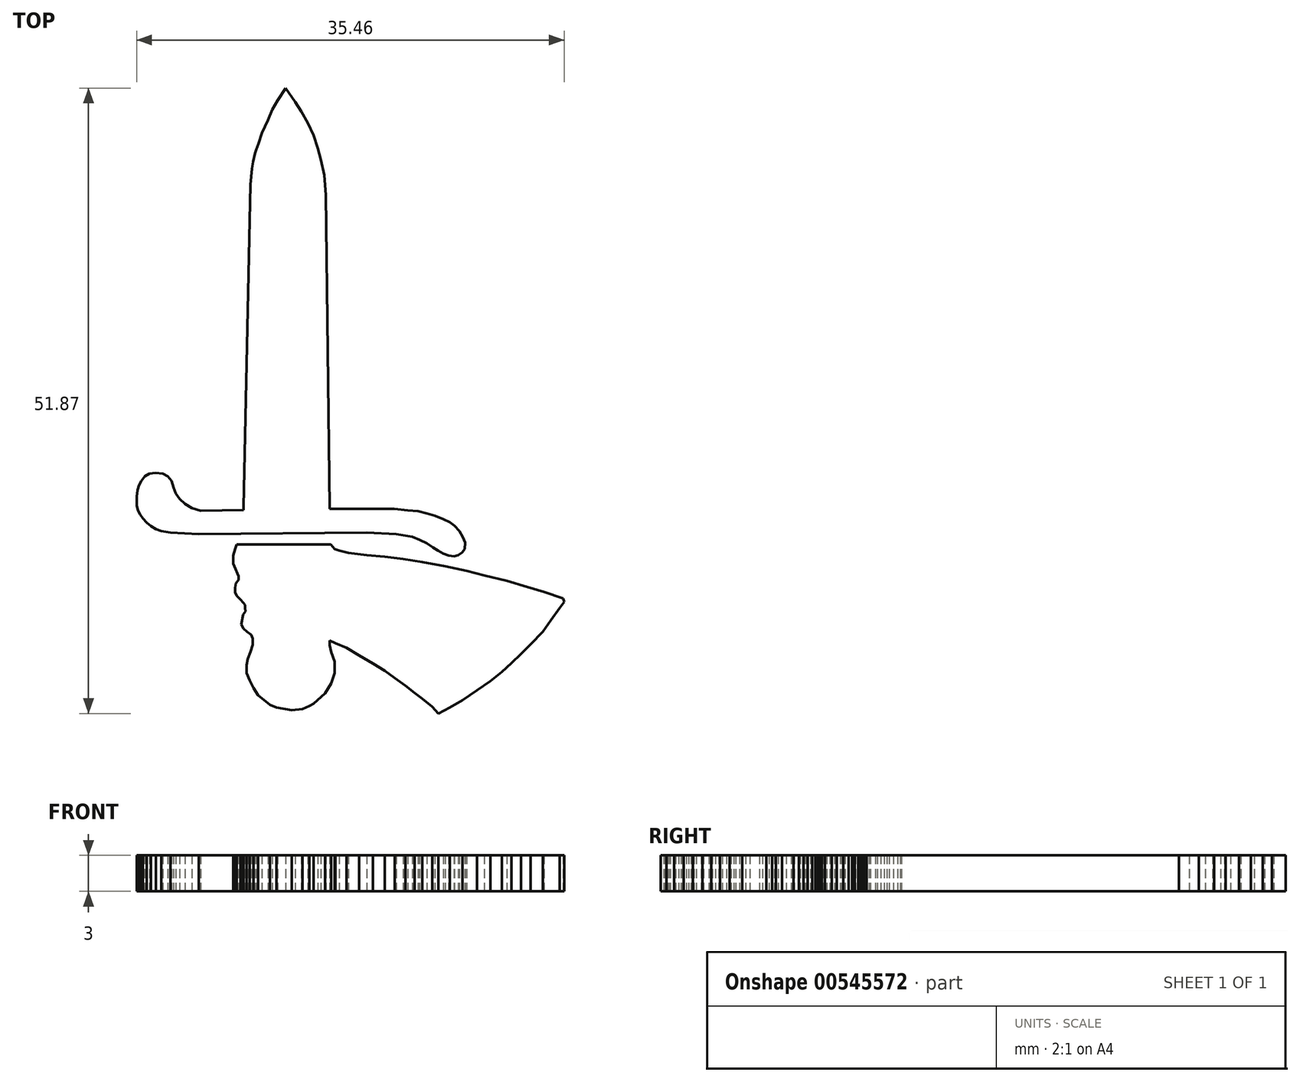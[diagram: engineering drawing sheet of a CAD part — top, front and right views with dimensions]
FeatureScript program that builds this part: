
annotation { "Feature Type Name" : "Feature", "Feature Type Description" : "" }
export const myFeature = defineFeature(function(context is Context, id is Id, definition is map)
    precondition{}
    {
        {
            var Q0;
            Q0=qCreatedBy(makeId("Top.planeOp"),FACE);
            var sketch = newSketch(context, id + "F0", { "sketchPlane" : qUnion([Q0])});
            skLineSegment(sketch, "E0", {"start": v(-69.97, -45.2) * mm, "end": v(-69.04, -44.33) * mm});
            skLineSegment(sketch, "E1", {"start": v(-69.04, -44.33) * mm, "end": v(-68.52, -43.52) * mm});
            skLineSegment(sketch, "E2", {"start": v(-68.52, -43.52) * mm, "end": v(-68.23, -42.65) * mm});
            skLineSegment(sketch, "E3", {"start": v(-68.23, -42.65) * mm, "end": v(-68.23, -41.72) * mm});
            skLineSegment(sketch, "E4", {"start": v(-68.23, -41.72) * mm, "end": v(-68.5, -40.9) * mm});
            skLineSegment(sketch, "E5", {"start": v(-68.5, -40.9) * mm, "end": v(-68.64, -40.36) * mm});
            skLineSegment(sketch, "E6", {"start": v(-68.64, -40.36) * mm, "end": v(-68.64, -39.95) * mm});
            skLineSegment(sketch, "E7", {"start": v(-68.64, -39.95) * mm, "end": v(-68.16, -40.17) * mm});
            skLineSegment(sketch, "E8", {"start": v(-68.16, -40.17) * mm, "end": v(-67.25, -40.56) * mm});
            skLineSegment(sketch, "E9", {"start": v(-67.25, -40.56) * mm, "end": v(-66.2, -41.2) * mm});
            skLineSegment(sketch, "E10", {"start": v(-66.2, -41.2) * mm, "end": v(-65.06, -41.86) * mm});
            skLineSegment(sketch, "E11", {"start": v(-65.06, -41.86) * mm, "end": v(-64.08, -42.47) * mm});
            skLineSegment(sketch, "E12", {"start": v(-64.08, -42.47) * mm, "end": v(-63.25, -43.07) * mm});
            skLineSegment(sketch, "E13", {"start": v(-63.25, -43.07) * mm, "end": v(-62.37, -43.7) * mm});
            skLineSegment(sketch, "E14", {"start": v(-62.37, -43.7) * mm, "end": v(-61.6, -44.31) * mm});
            skLineSegment(sketch, "E15", {"start": v(-61.6, -44.31) * mm, "end": v(-60.96, -44.8) * mm});
            skLineSegment(sketch, "E16", {"start": v(-60.96, -44.8) * mm, "end": v(-60.15, -45.47) * mm});
            skLineSegment(sketch, "E17", {"start": v(-60.15, -45.47) * mm, "end": v(-59.63, -46.02) * mm});
            skLineSegment(sketch, "E18", {"start": v(-59.63, -46.02) * mm, "end": v(-58.67, -45.52) * mm});
            skLineSegment(sketch, "E19", {"start": v(-58.67, -45.52) * mm, "end": v(-57.62, -44.9) * mm});
            skLineSegment(sketch, "E20", {"start": v(-57.62, -44.9) * mm, "end": v(-56.43, -44.1) * mm});
            skLineSegment(sketch, "E21", {"start": v(-56.43, -44.1) * mm, "end": v(-55.32, -43.33) * mm});
            skLineSegment(sketch, "E22", {"start": v(-55.32, -43.33) * mm, "end": v(-54.37, -42.56) * mm});
            skLineSegment(sketch, "E23", {"start": v(-54.37, -42.56) * mm, "end": v(-53.56, -41.83) * mm});
            skLineSegment(sketch, "E24", {"start": v(-53.56, -41.83) * mm, "end": v(-52.77, -41.08) * mm});
            skLineSegment(sketch, "E25", {"start": v(-52.77, -41.08) * mm, "end": v(-51.97, -40.28) * mm});
            skLineSegment(sketch, "E26", {"start": v(-51.97, -40.28) * mm, "end": v(-50.97, -39.24) * mm});
            skLineSegment(sketch, "E27", {"start": v(-50.97, -39.24) * mm, "end": v(-50.3, -38.29) * mm});
            skLineSegment(sketch, "E28", {"start": v(-50.3, -38.29) * mm, "end": v(-49.57, -37.25) * mm});
            skLineSegment(sketch, "E29", {"start": v(-49.57, -37.25) * mm, "end": v(-49.19, -36.77) * mm});
            skLineSegment(sketch, "E30", {"start": v(-49.19, -36.77) * mm, "end": v(-49.3, -36.47) * mm});
            skLineSegment(sketch, "E31", {"start": v(-49.3, -36.47) * mm, "end": v(-50.86, -35.94) * mm});
            skLineSegment(sketch, "E32", {"start": v(-50.86, -35.94) * mm, "end": v(-52.25, -35.52) * mm});
            skLineSegment(sketch, "E33", {"start": v(-52.25, -35.52) * mm, "end": v(-53.95, -35) * mm});
            skLineSegment(sketch, "E34", {"start": v(-53.95, -35) * mm, "end": v(-55.81, -34.55) * mm});
            skLineSegment(sketch, "E35", {"start": v(-55.81, -34.55) * mm, "end": v(-57.28, -34.18) * mm});
            skLineSegment(sketch, "E36", {"start": v(-57.28, -34.18) * mm, "end": v(-59.05, -33.81) * mm});
            skLineSegment(sketch, "E37", {"start": v(-59.05, -33.81) * mm, "end": v(-60.96, -33.44) * mm});
            skLineSegment(sketch, "E38", {"start": v(-60.96, -33.44) * mm, "end": v(-62.54, -33.18) * mm});
            skLineSegment(sketch, "E39", {"start": v(-62.54, -33.18) * mm, "end": v(-64.06, -33.02) * mm});
            skLineSegment(sketch, "E40", {"start": v(-64.06, -33.02) * mm, "end": v(-65.56, -32.9) * mm});
            skLineSegment(sketch, "E41", {"start": v(-65.56, -32.9) * mm, "end": v(-67.1, -32.7) * mm});
            skLineSegment(sketch, "E42", {"start": v(-67.1, -32.7) * mm, "end": v(-67.86, -32.51) * mm});
            skLineSegment(sketch, "E43", {"start": v(-67.86, -32.51) * mm, "end": v(-68.23, -32.36) * mm});
            skLineSegment(sketch, "E44", {"start": v(-68.23, -32.36) * mm, "end": v(-68.55, -31.99) * mm});
            skLineSegment(sketch, "E45", {"start": v(-68.55, -31.99) * mm, "end": v(-76.37, -31.99) * mm});
            skLineSegment(sketch, "E46", {"start": v(-76.37, -31.99) * mm, "end": v(-76.5, -32.39) * mm});
            skLineSegment(sketch, "E47", {"start": v(-76.5, -32.39) * mm, "end": v(-76.65, -32.9) * mm});
            skLineSegment(sketch, "E48", {"start": v(-76.65, -32.9) * mm, "end": v(-76.65, -33.22) * mm});
            skLineSegment(sketch, "E49", {"start": v(-76.65, -33.22) * mm, "end": v(-76.65, -33.59) * mm});
            skLineSegment(sketch, "E50", {"start": v(-76.65, -33.59) * mm, "end": v(-76.46, -34.01) * mm});
            skLineSegment(sketch, "E51", {"start": v(-76.46, -34.01) * mm, "end": v(-76.29, -34.41) * mm});
            skLineSegment(sketch, "E52", {"start": v(-76.29, -34.41) * mm, "end": v(-76.22, -34.62) * mm});
            skLineSegment(sketch, "E53", {"start": v(-76.22, -34.62) * mm, "end": v(-76.22, -34.95) * mm});
            skLineSegment(sketch, "E54", {"start": v(-76.22, -34.95) * mm, "end": v(-76.42, -35.2) * mm});
            skLineSegment(sketch, "E55", {"start": v(-76.42, -35.2) * mm, "end": v(-76.49, -35.6) * mm});
            skLineSegment(sketch, "E56", {"start": v(-76.49, -35.6) * mm, "end": v(-76.49, -35.96) * mm});
            skLineSegment(sketch, "E57", {"start": v(-76.49, -35.96) * mm, "end": v(-76.36, -36.26) * mm});
            skLineSegment(sketch, "E58", {"start": v(-76.36, -36.26) * mm, "end": v(-76.06, -36.57) * mm});
            skLineSegment(sketch, "E59", {"start": v(-76.06, -36.57) * mm, "end": v(-75.82, -36.83) * mm});
            skLineSegment(sketch, "E60", {"start": v(-75.82, -36.83) * mm, "end": v(-75.67, -37.01) * mm});
            skLineSegment(sketch, "E61", {"start": v(-75.67, -37.01) * mm, "end": v(-75.67, -37.25) * mm});
            skLineSegment(sketch, "E62", {"start": v(-75.67, -37.25) * mm, "end": v(-75.63, -37.56) * mm});
            skLineSegment(sketch, "E63", {"start": v(-75.63, -37.56) * mm, "end": v(-75.83, -37.81) * mm});
            skLineSegment(sketch, "E64", {"start": v(-75.83, -37.81) * mm, "end": v(-75.9, -38.2) * mm});
            skLineSegment(sketch, "E65", {"start": v(-75.9, -38.2) * mm, "end": v(-75.98, -38.63) * mm});
            skLineSegment(sketch, "E66", {"start": v(-75.98, -38.63) * mm, "end": v(-75.8, -38.97) * mm});
            skLineSegment(sketch, "E67", {"start": v(-75.8, -38.97) * mm, "end": v(-75.5, -39.24) * mm});
            skLineSegment(sketch, "E68", {"start": v(-75.5, -39.24) * mm, "end": v(-75.16, -39.48) * mm});
            skLineSegment(sketch, "E69", {"start": v(-75.16, -39.48) * mm, "end": v(-75.04, -39.8) * mm});
            skLineSegment(sketch, "E70", {"start": v(-75.04, -39.8) * mm, "end": v(-75.04, -40.3) * mm});
            skLineSegment(sketch, "E71", {"start": v(-75.04, -40.3) * mm, "end": v(-75.23, -40.9) * mm});
            skLineSegment(sketch, "E72", {"start": v(-75.23, -40.9) * mm, "end": v(-75.45, -41.47) * mm});
            skLineSegment(sketch, "E73", {"start": v(-75.45, -41.47) * mm, "end": v(-75.54, -42) * mm});
            skLineSegment(sketch, "E74", {"start": v(-75.54, -42) * mm, "end": v(-75.54, -42.66) * mm});
            skLineSegment(sketch, "E75", {"start": v(-75.54, -42.66) * mm, "end": v(-75.3, -43.27) * mm});
            skLineSegment(sketch, "E76", {"start": v(-75.3, -43.27) * mm, "end": v(-74.95, -43.9) * mm});
            skLineSegment(sketch, "E77", {"start": v(-74.95, -43.9) * mm, "end": v(-74.58, -44.51) * mm});
            skLineSegment(sketch, "E78", {"start": v(-74.58, -44.51) * mm, "end": v(-74.07, -44.91) * mm});
            skLineSegment(sketch, "E79", {"start": v(-74.07, -44.91) * mm, "end": v(-73.6, -45.29) * mm});
            skLineSegment(sketch, "E80", {"start": v(-73.6, -45.29) * mm, "end": v(-73.07, -45.52) * mm});
            skLineSegment(sketch, "E81", {"start": v(-73.07, -45.52) * mm, "end": v(-72.44, -45.63) * mm});
            skLineSegment(sketch, "E82", {"start": v(-72.44, -45.63) * mm, "end": v(-71.8, -45.75) * mm});
            skLineSegment(sketch, "E83", {"start": v(-71.8, -45.75) * mm, "end": v(-70.91, -45.63) * mm});
            skLineSegment(sketch, "E84", {"start": v(-70.91, -45.63) * mm, "end": v(-70.32, -45.4) * mm});
            skLineSegment(sketch, "E85", {"start": v(-70.32, -45.4) * mm, "end": v(-69.97, -45.2) * mm});
            skLineSegment(sketch, "E86", {"start": v(-68.64, -28.92) * mm, "end": v(-68.98, -3.02) * mm});
            skLineSegment(sketch, "E87", {"start": v(-68.98, -3.02) * mm, "end": v(-69.1, -1.36) * mm});
            skLineSegment(sketch, "E88", {"start": v(-69.1, -1.36) * mm, "end": v(-69.36, -0.1) * mm});
            skLineSegment(sketch, "E89", {"start": v(-69.36, -0.1) * mm, "end": v(-69.62, 0.86) * mm});
            skLineSegment(sketch, "E90", {"start": v(-69.62, 0.86) * mm, "end": v(-69.97, 1.95) * mm});
            skLineSegment(sketch, "E91", {"start": v(-69.97, 1.95) * mm, "end": v(-70.46, 2.95) * mm});
            skLineSegment(sketch, "E92", {"start": v(-70.46, 2.95) * mm, "end": v(-71, 3.92) * mm});
            skLineSegment(sketch, "E93", {"start": v(-71, 3.92) * mm, "end": v(-71.5, 4.7) * mm});
            skLineSegment(sketch, "E94", {"start": v(-71.5, 4.7) * mm, "end": v(-72.29, 5.85) * mm});
            skLineSegment(sketch, "E95", {"start": v(-72.29, 5.85) * mm, "end": v(-72.98, 4.84) * mm});
            skLineSegment(sketch, "E96", {"start": v(-72.98, 4.84) * mm, "end": v(-73.4, 4.08) * mm});
            skLineSegment(sketch, "E97", {"start": v(-73.4, 4.08) * mm, "end": v(-73.77, 3.23) * mm});
            skLineSegment(sketch, "E98", {"start": v(-73.77, 3.23) * mm, "end": v(-74.28, 2.13) * mm});
            skLineSegment(sketch, "E99", {"start": v(-74.28, 2.13) * mm, "end": v(-74.56, 1.25) * mm});
            skLineSegment(sketch, "E100", {"start": v(-74.56, 1.25) * mm, "end": v(-74.73, 0.75) * mm});
            skLineSegment(sketch, "E101", {"start": v(-74.73, 0.75) * mm, "end": v(-74.82, 0.45) * mm});
            skLineSegment(sketch, "E102", {"start": v(-74.82, 0.45) * mm, "end": v(-74.99, -0.23) * mm});
            skLineSegment(sketch, "E103", {"start": v(-74.99, -0.23) * mm, "end": v(-75.1, -0.83) * mm});
            skLineSegment(sketch, "E104", {"start": v(-75.1, -0.83) * mm, "end": v(-75.2, -2.15) * mm});
            skLineSegment(sketch, "E105", {"start": v(-75.2, -2.15) * mm, "end": v(-75.8, -28.9) * mm});
            skLineSegment(sketch, "E106", {"start": v(-75.8, -28.9) * mm, "end": v(-75.8, -29.14) * mm});
            skLineSegment(sketch, "E107", {"start": v(-75.8, -29.14) * mm, "end": v(-79.34, -29.19) * mm});
            skLineSegment(sketch, "E108", {"start": v(-79.34, -29.19) * mm, "end": v(-80.07, -28.96) * mm});
            skLineSegment(sketch, "E109", {"start": v(-80.07, -28.96) * mm, "end": v(-80.66, -28.61) * mm});
            skLineSegment(sketch, "E110", {"start": v(-80.66, -28.61) * mm, "end": v(-81.1, -28.2) * mm});
            skLineSegment(sketch, "E111", {"start": v(-81.1, -28.2) * mm, "end": v(-81.4, -27.77) * mm});
            skLineSegment(sketch, "E112", {"start": v(-81.4, -27.77) * mm, "end": v(-81.6, -27.25) * mm});
            skLineSegment(sketch, "E113", {"start": v(-81.6, -27.25) * mm, "end": v(-81.77, -26.72) * mm});
            skLineSegment(sketch, "E114", {"start": v(-81.77, -26.72) * mm, "end": v(-82.07, -26.36) * mm});
            skLineSegment(sketch, "E115", {"start": v(-82.07, -26.36) * mm, "end": v(-82.5, -26.1) * mm});
            skLineSegment(sketch, "E116", {"start": v(-82.5, -26.1) * mm, "end": v(-83.08, -26.05) * mm});
            skLineSegment(sketch, "E117", {"start": v(-83.08, -26.05) * mm, "end": v(-83.62, -26.12) * mm});
            skLineSegment(sketch, "E118", {"start": v(-83.62, -26.12) * mm, "end": v(-83.97, -26.36) * mm});
            skLineSegment(sketch, "E119", {"start": v(-83.97, -26.36) * mm, "end": v(-84.26, -26.72) * mm});
            skLineSegment(sketch, "E120", {"start": v(-84.26, -26.72) * mm, "end": v(-84.47, -27.07) * mm});
            skLineSegment(sketch, "E121", {"start": v(-84.47, -27.07) * mm, "end": v(-84.6, -27.47) * mm});
            skLineSegment(sketch, "E122", {"start": v(-84.6, -27.47) * mm, "end": v(-84.65, -28.04) * mm});
            skLineSegment(sketch, "E123", {"start": v(-84.65, -28.04) * mm, "end": v(-84.64, -28.75) * mm});
            skLineSegment(sketch, "E124", {"start": v(-84.64, -28.75) * mm, "end": v(-84.56, -29.17) * mm});
            skLineSegment(sketch, "E125", {"start": v(-84.56, -29.17) * mm, "end": v(-84.35, -29.5) * mm});
            skLineSegment(sketch, "E126", {"start": v(-84.35, -29.5) * mm, "end": v(-84.13, -29.84) * mm});
            skLineSegment(sketch, "E127", {"start": v(-84.13, -29.84) * mm, "end": v(-83.83, -30.2) * mm});
            skLineSegment(sketch, "E128", {"start": v(-83.83, -30.2) * mm, "end": v(-83.48, -30.48) * mm});
            skLineSegment(sketch, "E129", {"start": v(-83.48, -30.48) * mm, "end": v(-83.05, -30.7) * mm});
            skLineSegment(sketch, "E130", {"start": v(-83.05, -30.7) * mm, "end": v(-82.6, -30.89) * mm});
            skLineSegment(sketch, "E131", {"start": v(-82.6, -30.89) * mm, "end": v(-81.87, -31) * mm});
            skLineSegment(sketch, "E132", {"start": v(-81.87, -31) * mm, "end": v(-80.95, -31.05) * mm});
            skLineSegment(sketch, "E133", {"start": v(-80.95, -31.05) * mm, "end": v(-79.5, -31.12) * mm});
            skLineSegment(sketch, "E134", {"start": v(-79.5, -31.12) * mm, "end": v(-65.57, -31) * mm});
            skLineSegment(sketch, "E135", {"start": v(-65.57, -31) * mm, "end": v(-63.13, -31.13) * mm});
            skLineSegment(sketch, "E136", {"start": v(-63.13, -31.13) * mm, "end": v(-61.8, -31.37) * mm});
            skLineSegment(sketch, "E137", {"start": v(-61.8, -31.37) * mm, "end": v(-61.2, -31.6) * mm});
            skLineSegment(sketch, "E138", {"start": v(-61.2, -31.6) * mm, "end": v(-60.57, -31.9) * mm});
            skLineSegment(sketch, "E139", {"start": v(-60.57, -31.9) * mm, "end": v(-60.06, -32.25) * mm});
            skLineSegment(sketch, "E140", {"start": v(-60.06, -32.25) * mm, "end": v(-59.66, -32.5) * mm});
            skLineSegment(sketch, "E141", {"start": v(-59.66, -32.5) * mm, "end": v(-59.2, -32.75) * mm});
            skLineSegment(sketch, "E142", {"start": v(-59.2, -32.75) * mm, "end": v(-58.77, -32.92) * mm});
            skLineSegment(sketch, "E143", {"start": v(-58.77, -32.92) * mm, "end": v(-58.34, -32.99) * mm});
            skLineSegment(sketch, "E144", {"start": v(-58.34, -32.99) * mm, "end": v(-57.98, -32.87) * mm});
            skLineSegment(sketch, "E145", {"start": v(-57.98, -32.87) * mm, "end": v(-57.65, -32.65) * mm});
            skLineSegment(sketch, "E146", {"start": v(-57.65, -32.65) * mm, "end": v(-57.45, -32.39) * mm});
            skLineSegment(sketch, "E147", {"start": v(-57.45, -32.39) * mm, "end": v(-57.42, -31.83) * mm});
            skLineSegment(sketch, "E148", {"start": v(-57.42, -31.83) * mm, "end": v(-57.6, -31.4) * mm});
            skLineSegment(sketch, "E149", {"start": v(-57.6, -31.4) * mm, "end": v(-57.89, -30.88) * mm});
            skLineSegment(sketch, "E150", {"start": v(-57.89, -30.88) * mm, "end": v(-58.28, -30.44) * mm});
            skLineSegment(sketch, "E151", {"start": v(-58.28, -30.44) * mm, "end": v(-58.69, -30.14) * mm});
            skLineSegment(sketch, "E152", {"start": v(-58.69, -30.14) * mm, "end": v(-59.2, -29.9) * mm});
            skLineSegment(sketch, "E153", {"start": v(-59.2, -29.9) * mm, "end": v(-59.92, -29.62) * mm});
            skLineSegment(sketch, "E154", {"start": v(-59.92, -29.62) * mm, "end": v(-60.58, -29.43) * mm});
            skLineSegment(sketch, "E155", {"start": v(-60.58, -29.43) * mm, "end": v(-61.3, -29.23) * mm});
            skLineSegment(sketch, "E156", {"start": v(-61.3, -29.23) * mm, "end": v(-62.17, -29.15) * mm});
            skLineSegment(sketch, "E157", {"start": v(-62.17, -29.15) * mm, "end": v(-63.28, -29.03) * mm});
            skLineSegment(sketch, "E158", {"start": v(-63.28, -29.03) * mm, "end": v(-68.64, -29.03) * mm});
            skLineSegment(sketch, "E159", {"start": v(-68.64, -29.03) * mm, "end": v(-68.64, -28.92) * mm});
            skSolve(sketch);
        }
        {
            var Q0;
            Q0=makeQuery(id+"F0.imprint","IMPRINT",FACE,{"disambiguationData":[TD([[makeQuery(id+"F0.imprint","IMPRINT",EDGE,{"derivedFrom":sQuery(id+"F0.wireOp",EDGE,"E0")}),1.0]])]});
            var Q1;
            Q1=makeQuery(id+"F0.imprint","IMPRINT",FACE,{"disambiguationData":[TD([[makeQuery(id+"F0.imprint","IMPRINT",EDGE,{"derivedFrom":sQuery(id+"F0.wireOp",EDGE,"E86")}),1.0]])]});
            var Q2;
            Q2 = qConstructionFilter(qBodyType(qCreatedBy(id + "F0" ,EDGE), BodyType.WIRE), ConstructionObject.NO);
            extrude(context, id + "F1", {"entities" : qUnion([Q0, Q1]), "surfaceEntities" : qUnion([Q2]), "depth" : 3 * mm, "offsetDistance" : 25 * mm});
        }
    });
